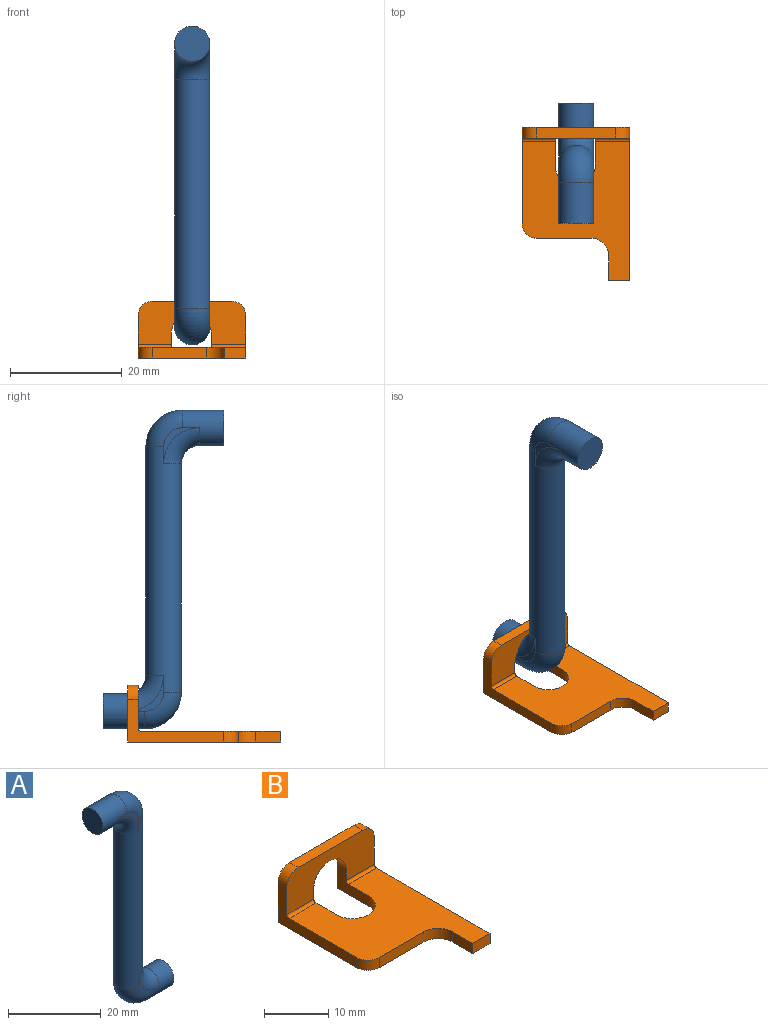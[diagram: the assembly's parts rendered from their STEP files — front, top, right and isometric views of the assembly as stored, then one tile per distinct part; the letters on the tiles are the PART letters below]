
ASSEMBLY  parts=2 mates=1
PART A: 13 faces, bbox 21.6x6.4x58.2 mm
  f0: plane 6.48x6.48mm, normal (0,1,0), area 6.5mm2, adj f6,f7,f8,f12
  f1: plane 6.48x6.48mm, normal (0,-1,0), area 6.5mm2, adj f6,f7,f8,f12
  f2: plane 6.35x6.35mm, normal (1,0,0), area 31.7mm2, adj f10
  f3: plane 6.35x6.35mm, normal (-1,0,0), area 31.7mm2, adj f6
  f4: plane 6.48x6.48mm, normal (0,-1,0), area 6.5mm2, adj f8,f9,f10,f11
  f5: plane 6.48x6.48mm, normal (0,1,0), area 6.5mm2, adj f8,f9,f10,f11
  f6: cylinder r=3.17mm len=7.37mm, axis (-1,0,0), area 116.5mm2, adj f0,f1,f3,f7,f12
  f7: torus R=3.43mm, axis (0,-1,0), area 85.4mm2, adj f0,f1,f6,f8
  f8: cylinder r=3.17mm len=43.94mm, axis (0,0,1), area 815.8mm2, adj f0,f1,f4,f5,f7,f9,f11,f12
  f9: torus R=6.48mm, axis (0,-1,0), area 69.8mm2, adj f4,f5,f8,f10
  f10: cylinder r=3.17mm len=7.37mm, axis (-1,0,0), area 116.5mm2, adj f2,f4,f5,f9,f11
  f11: torus R=3.43mm, axis (0,-1,0), area 85.4mm2, adj f4,f5,f8,f10
  f12: torus R=6.48mm, axis (0,-1,0), area 69.8mm2, adj f0,f1,f6,f8
PART B: 21 faces, bbox 19.3x27.4x10.2 mm
  f0: plane 19.3x10.16mm, normal (0,-1,0), area 112.6mm2, adj f1,f2,f3,f4,f5,f6,f7,f9
  f1: cylinder r=3.58mm len=7.14mm, axis (0,1,0), area 20.6mm2, adj f0,f2,f7,f8
  f2: plane 7.09x4.64mm, normal (-1,0,0), area 19mm2, adj f0,f1,f6,f8,f15,f16,f20
  f3: plane 27.43x7.62mm, normal (1,0,0), area 64mm2, adj f0,f6,f8,f9,f11,f16,f20
  f4: plane 14.22x1.93mm, normal (0,0,1), area 27.5mm2, adj f0,f8,f9,f10
  f5: plane 17.27x7.62mm, normal (-1,0,0), area 44.4mm2, adj f0,f6,f8,f10,f16,f17,f19
  f6: plane 27.43x19.3mm, normal (0,0,-1), area 342.9mm2, adj f0,f2,f3,f5,f7,f8,f11,f12
  f7: plane 4.64x1.93mm, normal (1,0,0), area 9mm2, adj f0,f1,f6,f8
  f8: plane 19.3x10.16mm, normal (0,1,0), area 142.2mm2, adj f1,f2,f3,f4,f5,f6,f7,f9
  f9: cylinder r=2.54mm len=2.54mm, axis (0,1,0), area 7.7mm2, adj f0,f3,f4,f8
  f10: cylinder r=2.54mm len=2.54mm, axis (0,1,0), area 7.7mm2, adj f0,f4,f5,f8
  f11: plane 3.81x1.93mm, normal (0,-1,0), area 7.4mm2, adj f3,f6,f12,f16
  f12: plane 4.45x1.93mm, normal (-1,0,0), area 8.6mm2, adj f6,f11,f16,f18
  f13: plane 9.78x1.93mm, normal (0,-1,0), area 18.9mm2, adj f6,f16,f17,f18
  f14: plane 5.17x2.44mm, normal (1,0,0), area 10mm2, adj f0,f6,f15,f16,f19
  f15: cylinder r=3.58mm len=7.15mm, axis (0,0,-1), area 20.9mm2, adj f2,f6,f14,f16
  f16: plane 24.99x19.3mm, normal (0,0,1), area 313.3mm2, adj f2,f3,f5,f11,f12,f13,f14,f15
  f17: cylinder r=2.54mm len=2.54mm, axis (0,0,1), area 7.7mm2, adj f5,f6,f13,f16
  f18: cylinder r=3.17mm len=3.18mm, axis (0,0,1), area 9.6mm2, adj f6,f12,f13,f16
  f19: cylinder r=0.51mm len=5.94mm, axis (1,0,0), area 4.7mm2, adj f0,f5,f14,f16
  f20: cylinder r=0.51mm len=6.21mm, axis (-1,0,0), area 5mm2, adj f0,f2,f3,f16
PLACE A rot(axis=(0,0,1),90deg) t=(-10.3,5.36,29.43)mm
PLACE B t=(-69.73,1.04,20.74)mm
MATE fastened A.f10 <-> B.f8  axis (0,1,0) through (-7.13,1.04,26.25)mm
